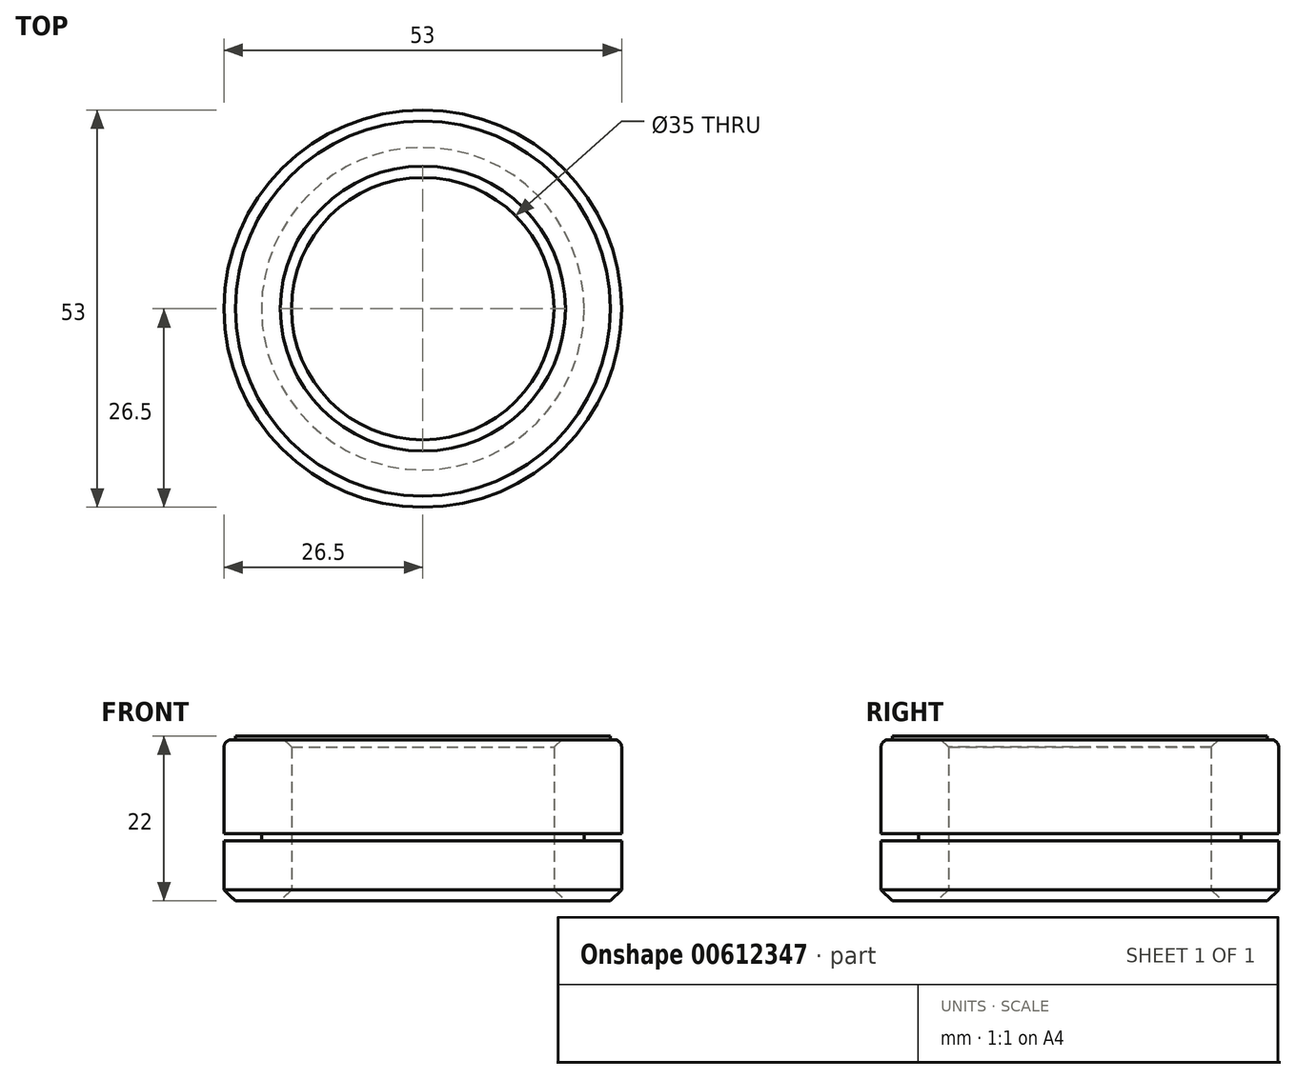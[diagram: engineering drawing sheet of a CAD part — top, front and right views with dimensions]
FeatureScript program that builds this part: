
annotation { "Feature Type Name" : "Feature", "Feature Type Description" : "" }
export const myFeature = defineFeature(function(context is Context, id is Id, definition is map)
    precondition{}
    {
        {
            var Q0;
            Q0=qCreatedBy(makeId("Front.planeOp"),FACE);
            var sketch = newSketch(context, id + "F0", { "sketchPlane" : qUnion([Q0])});
            skLineSegment(sketch, "E0", {"start": v(0, 0) * mm, "end": v(0, 4.14) * mm});
            skLineSegment(sketch, "E1", {"start": v(17.5, 0) * mm, "end": v(17.5, 22) * mm});
            skLineSegment(sketch, "E2", {"start": v(17.5, 22) * mm, "end": v(25, 22) * mm});
            skLineSegment(sketch, "E3", {"start": v(25, 22) * mm, "end": v(25, 21.5) * mm});
            skLineSegment(sketch, "E4", {"start": v(25, 21.5) * mm, "end": v(26.5, 21.5) * mm});
            skLineSegment(sketch, "E5", {"start": v(26.5, 21.5) * mm, "end": v(26.5, 9) * mm});
            skLineSegment(sketch, "E6", {"start": v(26.5, 9) * mm, "end": v(21.5, 9) * mm});
            skLineSegment(sketch, "E7", {"start": v(21.5, 9) * mm, "end": v(21.5, 8) * mm});
            skLineSegment(sketch, "E8", {"start": v(21.5, 8) * mm, "end": v(26.5, 8) * mm});
            skLineSegment(sketch, "E9", {"start": v(26.5, 8) * mm, "end": v(26.5, 0) * mm});
            skLineSegment(sketch, "E10", {"start": v(17.5, 0) * mm, "end": v(26.5, 0) * mm});
            skSolve(sketch);
        }
        {
            var Q0;
            Q0=makeQuery(id+"F0.imprint","IMPRINT",FACE,{"disambiguationData":[TD([[makeQuery(id+"F0.imprint","IMPRINT",EDGE,{"derivedFrom":sQuery(id+"F0.wireOp",EDGE,"E1")}),-1.0]])]});
            var Q1;
            Q1=sQuery(id+"F0.wireOp",EDGE,"E0");
            revolve(context, id + "F1", {"entities" : qUnion([Q0]), "axis" : qUnion([Q1]), "revolveType" : RevolveType.FULL});
        }
        {
            var Q0;
            Q0=makeQuery(id+"F1.opRevolve","SWEPT_EDGE",EDGE,{"disambiguationData":[OSD([sQuery(id+"F0.wireOp",EDGE,"E4"),sQuery(id+"F0.wireOp",EDGE,"E5")])]});
            fillet(context, id + "F2", {"entities" : qUnion([Q0]), "radius" : 1 * mm, "tangentPropagation" : true, "allowEdgeOverflow" : false});
        }
        {
            var Q0;
            Q0=makeQuery(id+"F1.opRevolve","SWEPT_EDGE",EDGE,{"disambiguationData":[OSD([sQuery(id+"F0.wireOp",EDGE,"E9"),sQuery(id+"F0.wireOp",EDGE,"E10")])]});
            var Q1;
            Q1=makeQuery(id+"F1.opRevolve","SWEPT_EDGE",EDGE,{"disambiguationData":[OSD([sQuery(id+"F0.wireOp",EDGE,"E1"),sQuery(id+"F0.wireOp",EDGE,"E2")])]});
            var Q2;
            Q2=makeQuery(id+"F1.opRevolve","SWEPT_EDGE",EDGE,{"disambiguationData":[OSD([sQuery(id+"F0.wireOp",EDGE,"E1"),sQuery(id+"F0.wireOp",EDGE,"E10")])]});
            chamfer(context, id + "F3", {"entities" : qUnion([Q0, Q1, Q2]), "width" : 1.5 * mm, "tangentPropagation" : true});
        }
    });
